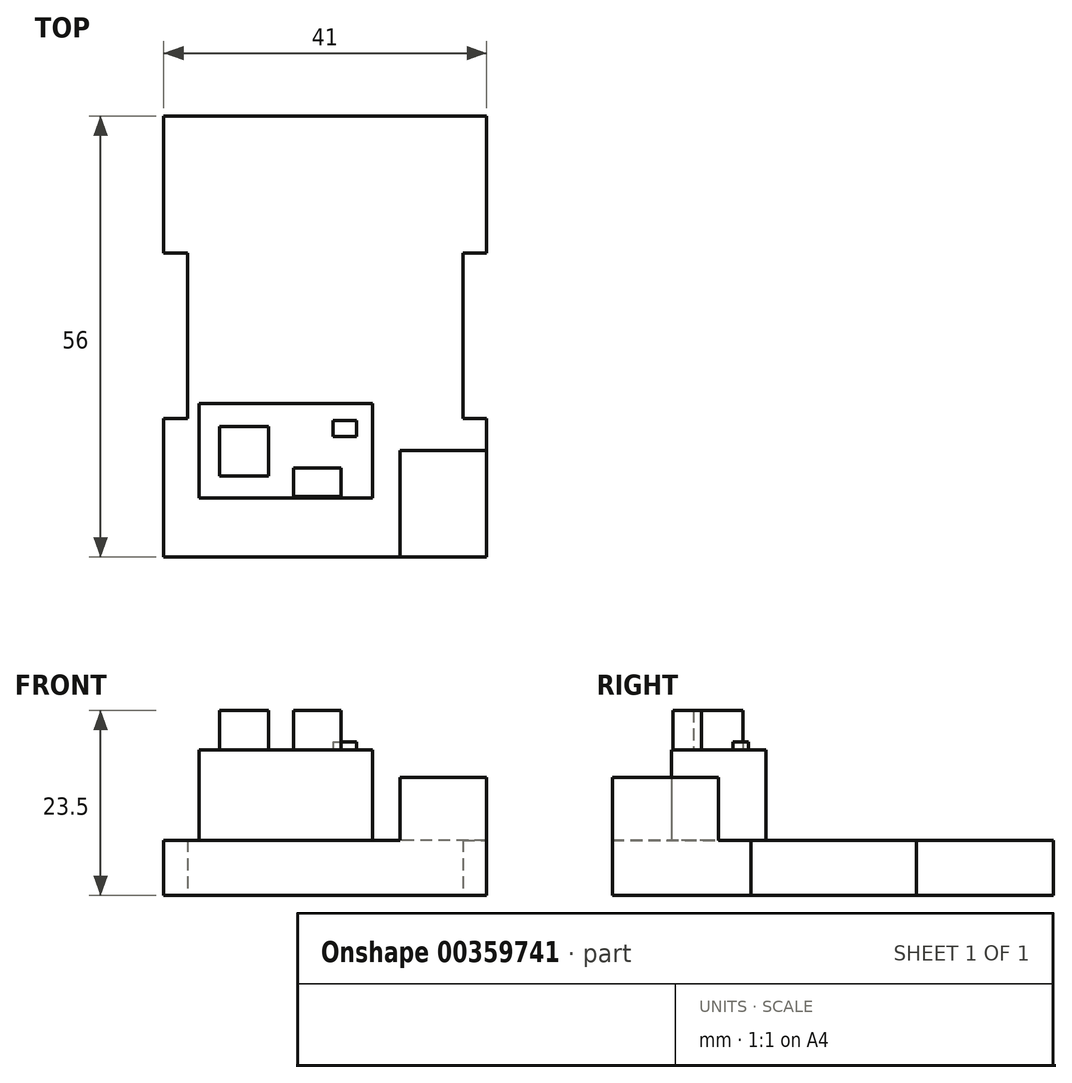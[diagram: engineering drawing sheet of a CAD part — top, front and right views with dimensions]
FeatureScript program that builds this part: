
annotation { "Feature Type Name" : "Feature", "Feature Type Description" : "" }
export const myFeature = defineFeature(function(context is Context, id is Id, definition is map)
    precondition{}
    {
        {
            var Q0;
            Q0=qCreatedBy(makeId("Top.planeOp"),FACE);
            var sketch = newSketch(context, id + "F0", { "sketchPlane" : qUnion([Q0])});
            skLineSegment(sketch, "E0.bottom", {"start": v(-36.1, 40.1) * mm, "end": v(4.9, 40.1) * mm});
            skLineSegment(sketch, "E0.top", {"start": v(-36.1, -15.9) * mm, "end": v(4.9, -15.9) * mm});
            skLineSegment(sketch, "E0.left", {"start": v(-36.1, 40.1) * mm, "end": v(-36.1, 22.7) * mm});
            skLineSegment(sketch, "E0.right", {"start": v(4.9, 40.1) * mm, "end": v(4.9, 22.7) * mm});
            skLineSegment(sketch, "E1", {"start": v(-36.1, 1.7) * mm, "end": v(-33.1, 1.7) * mm});
            skLineSegment(sketch, "E2", {"start": v(-36.1, 22.7) * mm, "end": v(-33.1, 22.7) * mm});
            skLineSegment(sketch, "E3", {"start": v(-33.1, 1.7) * mm, "end": v(-33.1, 22.7) * mm});
            skLineSegment(sketch, "E4", {"start": v(1.9, 22.7) * mm, "end": v(1.9, 1.7) * mm});
            skLineSegment(sketch, "E5.trimOffspring", {"start": v(1.9, 22.7) * mm, "end": v(4.9, 22.7) * mm});
            skLineSegment(sketch, "E6.trimOffspring", {"start": v(1.9, 1.7) * mm, "end": v(4.9, 1.7) * mm});
            skLineSegment(sketch, "E7.trimOffspring", {"start": v(-36.1, 1.7) * mm, "end": v(-36.1, -15.9) * mm});
            skLineSegment(sketch, "E8.trimOffspring", {"start": v(4.9, 1.7) * mm, "end": v(4.9, -15.9) * mm});
            skSolve(sketch);
        }
        {
            var Q0;
            Q0 = qSketchRegion(id + "F0", true);
            extrude(context, id + "F1", {"entities" : qUnion([Q0]), "depth" : 7 * mm});
        }
        {
            var Q0;
            Q0=makeQuery(id+"F1.opExtrude","CAP_FACE",FACE,{"disambiguationData":[OSD([sQuery(id+"F0.wireOp",EDGE,"E0.bottom"),sQuery(id+"F0.wireOp",EDGE,"E0.top"),sQuery(id+"F0.wireOp",EDGE,"E0.left"),sQuery(id+"F0.wireOp",EDGE,"E0.right"),sQuery(id+"F0.wireOp",EDGE,"E1"),sQuery(id+"F0.wireOp",EDGE,"E2"),sQuery(id+"F0.wireOp",EDGE,"E3"),sQuery(id+"F0.wireOp",EDGE,"E4"),sQuery(id+"F0.wireOp",EDGE,"E5.trimOffspring"),sQuery(id+"F0.wireOp",EDGE,"E6.trimOffspring"),sQuery(id+"F0.wireOp",EDGE,"E7.trimOffspring"),sQuery(id+"F0.wireOp",EDGE,"E8.trimOffspring")])],"isStart":false});
            var sketch = newSketch(context, id + "F2", { "sketchPlane" : qUnion([Q0])});
            skLineSegment(sketch, "E9.bottom", {"start": v(4.9, -15.9) * mm, "end": v(-6.1, -15.9) * mm});
            skLineSegment(sketch, "E9.top", {"start": v(4.9, -2.4) * mm, "end": v(-6.1, -2.4) * mm});
            skLineSegment(sketch, "E9.left", {"start": v(4.9, -15.9) * mm, "end": v(4.9, -2.4) * mm});
            skLineSegment(sketch, "E9.right", {"start": v(-6.1, -15.9) * mm, "end": v(-6.1, -2.4) * mm});
            skSolve(sketch);
        }
        {
            var Q0;
            Q0=makeQuery(id+"F2.imprint","IMPRINT",FACE,{"disambiguationData":[TD([[makeQuery(id+"F2.imprint","IMPRINT",EDGE,{"derivedFrom":sQuery(id+"F2.wireOp",EDGE,"E9.bottom")}),1.0]])]});
            extrude(context, id + "F3", {"entities" : qUnion([Q0]), "operationType" : NewBodyOperationType.ADD, "depth" : 8 * mm});
        }
        {
            var Q0;
            Q0=makeQuery(id+"F1.opExtrude","CAP_FACE",FACE,{"disambiguationData":[OSD([sQuery(id+"F0.wireOp",EDGE,"E0.bottom"),sQuery(id+"F0.wireOp",EDGE,"E0.top"),sQuery(id+"F0.wireOp",EDGE,"E0.left"),sQuery(id+"F0.wireOp",EDGE,"E0.right"),sQuery(id+"F0.wireOp",EDGE,"E1"),sQuery(id+"F0.wireOp",EDGE,"E2"),sQuery(id+"F0.wireOp",EDGE,"E3"),sQuery(id+"F0.wireOp",EDGE,"E4"),sQuery(id+"F0.wireOp",EDGE,"E5.trimOffspring"),sQuery(id+"F0.wireOp",EDGE,"E6.trimOffspring"),sQuery(id+"F0.wireOp",EDGE,"E7.trimOffspring"),sQuery(id+"F0.wireOp",EDGE,"E8.trimOffspring")])],"isStart":false});
            var sketch = newSketch(context, id + "F4", { "sketchPlane" : qUnion([Q0])});
            skLineSegment(sketch, "E10.bottom", {"start": v(-31.6, 3.6) * mm, "end": v(-9.6, 3.6) * mm});
            skLineSegment(sketch, "E10.top", {"start": v(-31.6, -8.4) * mm, "end": v(-9.6, -8.4) * mm});
            skLineSegment(sketch, "E10.left", {"start": v(-31.6, 3.6) * mm, "end": v(-31.6, -8.4) * mm});
            skLineSegment(sketch, "E10.right", {"start": v(-9.6, 3.6) * mm, "end": v(-9.6, -8.4) * mm});
            skSolve(sketch);
        }
        {
            var Q0;
            Q0=makeQuery(id+"F4.imprint","IMPRINT",FACE,{"disambiguationData":[TD([[makeQuery(id+"F4.imprint","IMPRINT",EDGE,{"derivedFrom":sQuery(id+"F4.wireOp",EDGE,"E10.bottom")}),-1.0]])]});
            extrude(context, id + "F5", {"entities" : qUnion([Q0]), "operationType" : NewBodyOperationType.ADD, "depth" : 11.5 * mm});
        }
        {
            var Q0;
            Q0=makeQuery(id+"F5.opExtrude","CAP_FACE",FACE,{"disambiguationData":[OSD([sQuery(id+"F4.wireOp",EDGE,"E10.bottom"),sQuery(id+"F4.wireOp",EDGE,"E10.top"),sQuery(id+"F4.wireOp",EDGE,"E10.left"),sQuery(id+"F4.wireOp",EDGE,"E10.right")])],"isStart":false});
            var sketch = newSketch(context, id + "F6", { "sketchPlane" : qUnion([Q0])});
            skLineSegment(sketch, "E11.bottom", {"start": v(-29, 0.7) * mm, "end": v(-22.8, 0.7) * mm});
            skLineSegment(sketch, "E11.top", {"start": v(-29, -5.6) * mm, "end": v(-22.8, -5.6) * mm});
            skLineSegment(sketch, "E11.left", {"start": v(-29, 0.7) * mm, "end": v(-29, -5.6) * mm});
            skLineSegment(sketch, "E11.right", {"start": v(-22.8, 0.7) * mm, "end": v(-22.8, -5.6) * mm});
            skLineSegment(sketch, "E12.bottom", {"start": v(-19.6, -4.6) * mm, "end": v(-13.6, -4.6) * mm});
            skLineSegment(sketch, "E12.top", {"start": v(-19.6, -8.2) * mm, "end": v(-13.6, -8.2) * mm});
            skLineSegment(sketch, "E12.left", {"start": v(-19.6, -4.6) * mm, "end": v(-19.6, -8.2) * mm});
            skLineSegment(sketch, "E12.right", {"start": v(-13.6, -4.6) * mm, "end": v(-13.6, -8.2) * mm});
            skLineSegment(sketch, "E13.bottom", {"start": v(-14.6, 1.4) * mm, "end": v(-11.6, 1.4) * mm});
            skLineSegment(sketch, "E13.top", {"start": v(-14.6, -0.6) * mm, "end": v(-11.6, -0.6) * mm});
            skLineSegment(sketch, "E13.left", {"start": v(-14.6, 1.4) * mm, "end": v(-14.6, -0.6) * mm});
            skLineSegment(sketch, "E13.right", {"start": v(-11.6, 1.4) * mm, "end": v(-11.6, -0.6) * mm});
            skSolve(sketch);
        }
        {
            var Q0;
            Q0=makeQuery(id+"F6.imprint","IMPRINT",FACE,{"disambiguationData":[TD([[makeQuery(id+"F6.imprint","IMPRINT",EDGE,{"derivedFrom":sQuery(id+"F6.wireOp",EDGE,"E13.bottom")}),-1.0]])]});
            extrude(context, id + "F7", {"entities" : qUnion([Q0]), "operationType" : NewBodyOperationType.ADD, "depth" : 1 * mm});
        }
        {
            var Q0;
            Q0=makeQuery(id+"F6.imprint","IMPRINT",FACE,{"disambiguationData":[TD([[makeQuery(id+"F6.imprint","IMPRINT",EDGE,{"derivedFrom":sQuery(id+"F6.wireOp",EDGE,"E11.bottom")}),-1.0]])]});
            var Q1;
            Q1=makeQuery(id+"F6.imprint","IMPRINT",FACE,{"disambiguationData":[TD([[makeQuery(id+"F6.imprint","IMPRINT",EDGE,{"derivedFrom":sQuery(id+"F6.wireOp",EDGE,"E12.bottom")}),-1.0]])]});
            extrude(context, id + "F8", {"entities" : qUnion([Q0, Q1]), "operationType" : NewBodyOperationType.ADD, "depth" : 5 * mm});
        }
    });
